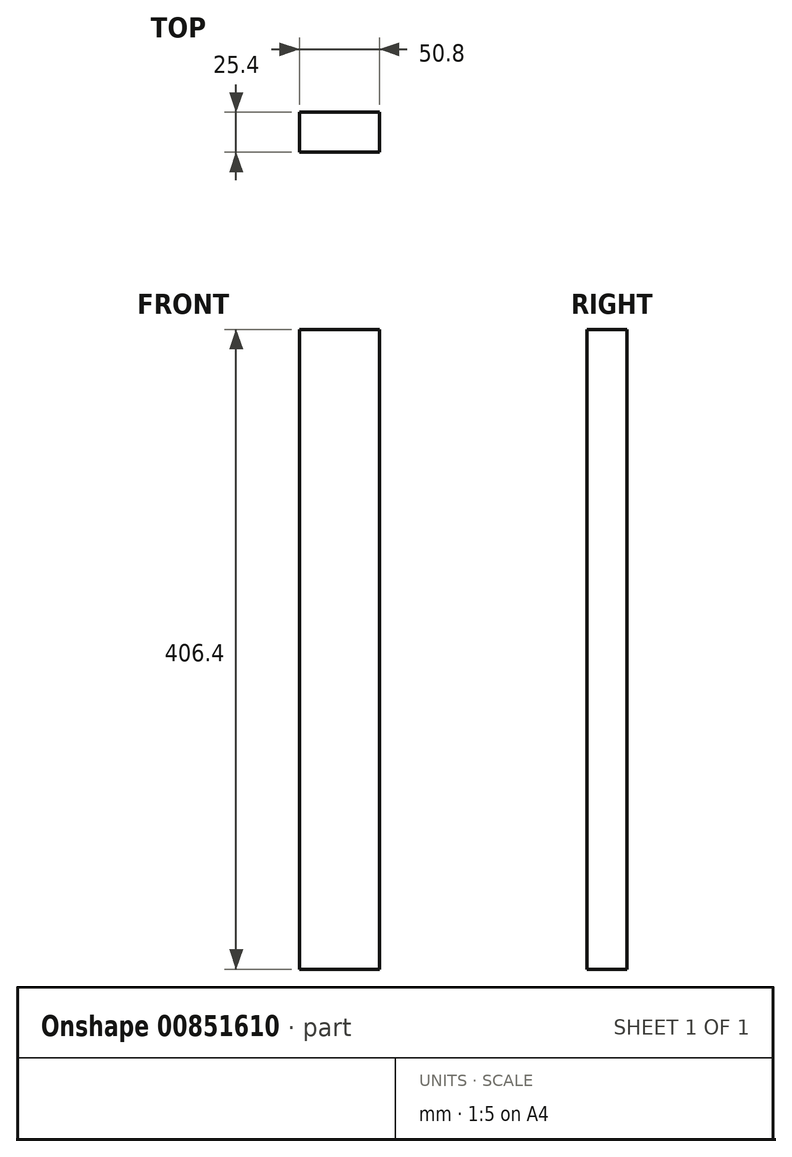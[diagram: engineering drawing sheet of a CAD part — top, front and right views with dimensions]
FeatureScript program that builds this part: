
annotation { "Feature Type Name" : "Feature", "Feature Type Description" : "" }
export const myFeature = defineFeature(function(context is Context, id is Id, definition is map)
    precondition{}
    {
        {
            var Q0;
            Q0=qCreatedBy(makeId("Front.planeOp"),FACE);
            var sketch = newSketch(context, id + "F0", { "sketchPlane" : qUnion([Q0])});
            skLineSegment(sketch, "E0", {"start": v(-50.8, 117.73) * mm, "end": v(0, 117.73) * mm});
            skLineSegment(sketch, "E1", {"start": v(-50.8, 117.73) * mm, "end": v(-50.8, -288.67) * mm});
            skLineSegment(sketch, "E2", {"start": v(0, 117.73) * mm, "end": v(0, -288.67) * mm});
            skLineSegment(sketch, "E3", {"start": v(0, -288.67) * mm, "end": v(-50.8, -288.67) * mm});
            skSolve(sketch);
        }
        {
            var Q0;
            Q0 = qSketchRegion(id + "F0", true);
            extrude(context, id + "F1", {"entities" : qUnion([Q0]), "depth" : 25.4 * mm, "offsetDistance" : 25.4 * mm});
        }
    });
